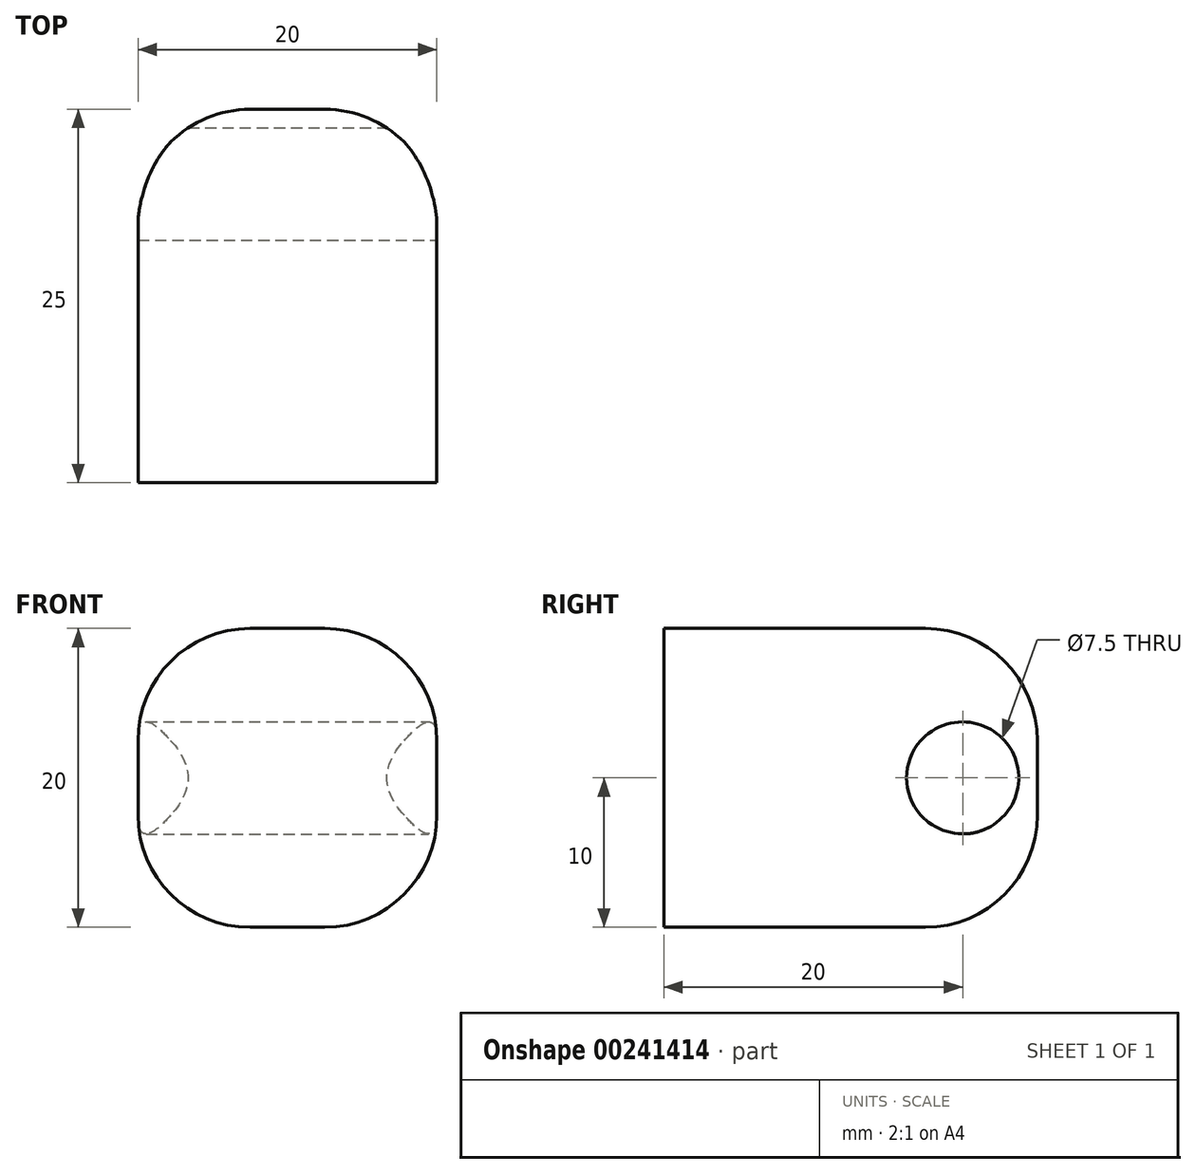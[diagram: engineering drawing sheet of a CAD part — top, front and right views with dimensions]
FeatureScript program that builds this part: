
annotation { "Feature Type Name" : "Feature", "Feature Type Description" : "" }
export const myFeature = defineFeature(function(context is Context, id is Id, definition is map)
    precondition{}
    {
        {
            var Q0;
            Q0=qCreatedBy(makeId("Front.planeOp"),FACE);
            var sketch = newSketch(context, id + "F0", { "sketchPlane" : qUnion([Q0])});
            skPoint(sketch, "E0.middle", {"position": v(0, 0) * mm});
            skLineSegment(sketch, "E1.bottom", {"start": v(10, -10) * mm, "end": v(-10, -10) * mm});
            skLineSegment(sketch, "E1.top", {"start": v(10, 10) * mm, "end": v(-10, 10) * mm});
            skLineSegment(sketch, "E1.left", {"start": v(10, -10) * mm, "end": v(10, 10) * mm});
            skLineSegment(sketch, "E1.right", {"start": v(-10, -10) * mm, "end": v(-10, 10) * mm});
            skSolve(sketch);
        }
        {
            var Q0;
            Q0 = qSketchRegion(id + "F0", true);
            extrude(context, id + "F1", {"entities" : qUnion([Q0]), "depth" : 25 * mm});
        }
        {
            var Q0;
            Q0=qCreatedBy(makeId("Right.planeOp"),FACE);
            var sketch = newSketch(context, id + "F2", { "sketchPlane" : qUnion([Q0])});
            skCircle(sketch, "E2", {"center": v(-5, 0) * mm, "radius": 3.75 * mm});
            skSolve(sketch);
        }
        {
            var Q0;
            Q0 = qSketchRegion(id + "F2", true);
            extrude(context, id + "F3", {"entities" : qUnion([Q0]), "operationType" : NewBodyOperationType.REMOVE, "endBound" : BoundingType.SYMMETRIC, "oppositeDirection" : true, "depth" : 50 * mm});
        }
        {
            var Q0;
            Q0=makeQuery(id+"F1.opExtrude","CAP_EDGE",EDGE,{"disambiguationData":[OSD([sQuery(id+"F0.wireOp",EDGE,"E1.top")])],"isStart":true});
            var Q1;
            Q1=makeQuery(id+"F1.opExtrude","CAP_EDGE",EDGE,{"disambiguationData":[OSD([sQuery(id+"F0.wireOp",EDGE,"E1.bottom")])],"isStart":true});
            fillet(context, id + "F4", {"entities" : qUnion([Q0, Q1]), "radius" : 7.5 * mm, "tangentPropagation" : true, "allowEdgeOverflow" : false});
        }
        {
            var Q0;
            Q0=makeQuery(id+"F1.opExtrude","SWEPT_EDGE",EDGE,{"disambiguationData":[OSD([sQuery(id+"F0.wireOp",EDGE,"E1.top"),sQuery(id+"F0.wireOp",EDGE,"E1.right")])]});
            var Q1;
            Q1=makeQuery(id+"F1.opExtrude","SWEPT_EDGE",EDGE,{"disambiguationData":[OSD([sQuery(id+"F0.wireOp",EDGE,"E1.top"),sQuery(id+"F0.wireOp",EDGE,"E1.left")])]});
            fillet(context, id + "F5", {"entities" : qUnion([Q0, Q1]), "radius" : 7.5 * mm, "tangentPropagation" : true, "allowEdgeOverflow" : false});
        }
    });
